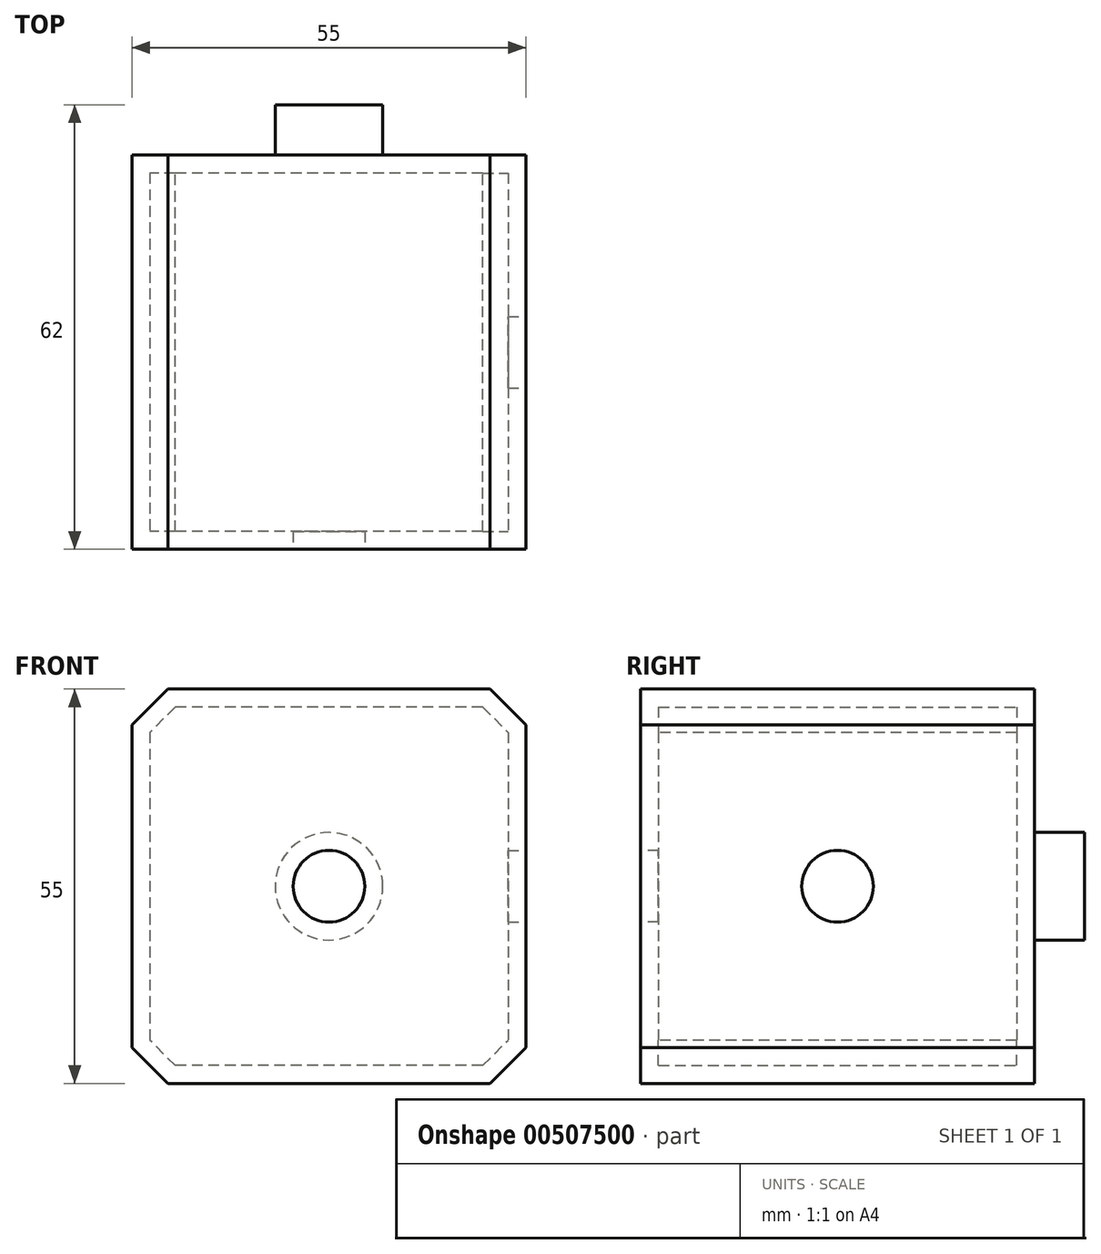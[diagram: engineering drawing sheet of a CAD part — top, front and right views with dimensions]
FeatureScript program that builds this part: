
annotation { "Feature Type Name" : "Feature", "Feature Type Description" : "" }
export const myFeature = defineFeature(function(context is Context, id is Id, definition is map)
    precondition{}
    {
        {
            var Q0;
            Q0=qCreatedBy(makeId("Front.planeOp"),FACE);
            var sketch = newSketch(context, id + "F0", { "sketchPlane" : qUnion([Q0])});
            skLineSegment(sketch, "E0.bottom", {"start": v(27.5, 27.5) * mm, "end": v(-27.5, 27.5) * mm});
            skLineSegment(sketch, "E0.top", {"start": v(27.5, -27.5) * mm, "end": v(-27.5, -27.5) * mm});
            skLineSegment(sketch, "E0.left", {"start": v(27.5, 27.5) * mm, "end": v(27.5, -27.5) * mm});
            skLineSegment(sketch, "E0.right", {"start": v(-27.5, 27.5) * mm, "end": v(-27.5, -27.5) * mm});
            skPoint(sketch, "E0.middle", {"position": v(0, 0) * mm});
            skSolve(sketch);
        }
        {
            var Q0;
            Q0=qSketchRegion(id+"F0",true);
            extrude(context, id + "F1", {"entities" : qUnion([Q0]), "depth" : 55 * mm});
        }
        {
            var Q0;
            Q0=makeQuery(id+"F1.opExtrude","SWEPT_EDGE",EDGE,{"disambiguationData":[OSD([sQuery(id+"F0.wireOp",EDGE,"E0.bottom"),sQuery(id+"F0.wireOp",EDGE,"E0.left")])]});
            var Q1;
            Q1=makeQuery(id+"F1.opExtrude","SWEPT_EDGE",EDGE,{"disambiguationData":[OSD([sQuery(id+"F0.wireOp",EDGE,"E0.bottom"),sQuery(id+"F0.wireOp",EDGE,"E0.right")])]});
            var Q2;
            Q2=makeQuery(id+"F1.opExtrude","SWEPT_EDGE",EDGE,{"disambiguationData":[OSD([sQuery(id+"F0.wireOp",EDGE,"E0.top"),sQuery(id+"F0.wireOp",EDGE,"E0.left")])]});
            var Q3;
            Q3=makeQuery(id+"F1.opExtrude","SWEPT_EDGE",EDGE,{"disambiguationData":[OSD([sQuery(id+"F0.wireOp",EDGE,"E0.top"),sQuery(id+"F0.wireOp",EDGE,"E0.right")])]});
            chamfer(context, id + "F2", {"entities" : qUnion([Q0, Q1, Q2, Q3]), "width" : 5 * mm, "tangentPropagation" : true});
        }
        {
            var Q0;
            Q0=makeQuery(id+"F1.opExtrude","CAP_FACE",FACE,{"disambiguationData":[OSD([sQuery(id+"F0.wireOp",EDGE,"E0.bottom"),sQuery(id+"F0.wireOp",EDGE,"E0.top"),sQuery(id+"F0.wireOp",EDGE,"E0.left"),sQuery(id+"F0.wireOp",EDGE,"E0.right")])],"isStart":false});
            var sketch = newSketch(context, id + "F3", { "sketchPlane" : qUnion([Q0])});
            skCircle(sketch, "E1", {"center": v(0, 0) * mm, "radius": 5 * mm});
            skSolve(sketch);
        }
        {
            var Q0;
            Q0=makeQuery(id+"F1.opExtrude","SWEPT_FACE",FACE,{"disambiguationData":[OSD([sQuery(id+"F0.wireOp",EDGE,"E0.left")])]});
            var sketch = newSketch(context, id + "F4", { "sketchPlane" : qUnion([Q0])});
            skCircle(sketch, "E2", {"center": v(-27.5, 0) * mm, "radius": 5 * mm});
            skPoint(sketch, "E2.centerSnap0", {"position": v(-27.5, 22.5) * mm});
            skSolve(sketch);
        }
        {
            var Q0;
            Q0=makeQuery(id+"F1.opExtrude","CAP_FACE",FACE,{"disambiguationData":[OSD([sQuery(id+"F0.wireOp",EDGE,"E0.bottom"),sQuery(id+"F0.wireOp",EDGE,"E0.top"),sQuery(id+"F0.wireOp",EDGE,"E0.left"),sQuery(id+"F0.wireOp",EDGE,"E0.right")])],"isStart":false});
            shell(context, id + "F5", {"entities" : qUnion([Q0]), "thickness" : 2.5 * mm});
        }
        {
            var Q0;
            Q0=makeQuery(id+"F3.imprint","IMPRINT",FACE,{"disambiguationData":[TD([[makeQuery(id+"F3.imprint","IMPRINT",EDGE,{"derivedFrom":sQuery(id+"F3.wireOp",EDGE,"E1")}),-1.0]])]});
            var sketch = newSketch(context, id + "F6", { "sketchPlane" : qUnion([Q0])});
            skLineSegment(sketch, "E3.bottom", {"start": v(22.5, 27.5) * mm, "end": v(-22.5, 27.5) * mm});
            skLineSegment(sketch, "E3.top", {"start": v(22.5, -27.5) * mm, "end": v(-22.5, -27.5) * mm});
            skLineSegment(sketch, "E3.left", {"start": v(27.5, 22.5) * mm, "end": v(27.5, -22.5) * mm});
            skLineSegment(sketch, "E3.right", {"start": v(-27.5, 22.5) * mm, "end": v(-27.5, -22.5) * mm});
            skPoint(sketch, "E3.middle", {"position": v(0, 0) * mm});
            skLineSegment(sketch, "E4", {"start": v(-22.5, 27.5) * mm, "end": v(-27.5, 22.5) * mm});
            skLineSegment(sketch, "E5", {"start": v(-22.5, -27.5) * mm, "end": v(-27.5, -22.5) * mm});
            skLineSegment(sketch, "E6", {"start": v(22.5, -27.5) * mm, "end": v(27.5, -22.5) * mm});
            skLineSegment(sketch, "E7", {"start": v(27.5, 22.5) * mm, "end": v(22.5, 27.5) * mm});
            skSolve(sketch);
        }
        {
            var Q0;
            Q0=qSketchRegion(id+"F6",true);
            extrude(context, id + "F7", {"entities" : qUnion([Q0]), "operationType" : NewBodyOperationType.ADD, "oppositeDirection" : true, "depth" : 2.5 * mm});
        }
        {
            var Q0;
            Q0=qSketchRegion(id+"F4",true);
            extrude(context, id + "F8", {"entities" : qUnion([Q0]), "operationType" : NewBodyOperationType.REMOVE, "oppositeDirection" : true, "depth" : 2.5 * mm});
        }
        {
            var Q0;
            Q0=qSketchRegion(id+"F3",true);
            extrude(context, id + "F9", {"entities" : qUnion([Q0]), "operationType" : NewBodyOperationType.REMOVE, "oppositeDirection" : true, "depth" : 2.5 * mm});
        }
        {
            var Q0;
            Q0=makeQuery(id+"F1.opExtrude","CAP_FACE",FACE,{"disambiguationData":[OSD([sQuery(id+"F0.wireOp",EDGE,"E0.bottom"),sQuery(id+"F0.wireOp",EDGE,"E0.top"),sQuery(id+"F0.wireOp",EDGE,"E0.left"),sQuery(id+"F0.wireOp",EDGE,"E0.right")])],"isStart":true});
            var sketch = newSketch(context, id + "F10", { "sketchPlane" : qUnion([Q0])});
            skCircle(sketch, "E8", {"center": v(0, 0) * mm, "radius": 7.5 * mm});
            skSolve(sketch);
        }
        {
            var Q0;
            Q0=qSketchRegion(id+"F10",true);
            extrude(context, id + "F11", {"entities" : qUnion([Q0]), "operationType" : NewBodyOperationType.ADD, "depth" : 7 * mm});
        }
    });
